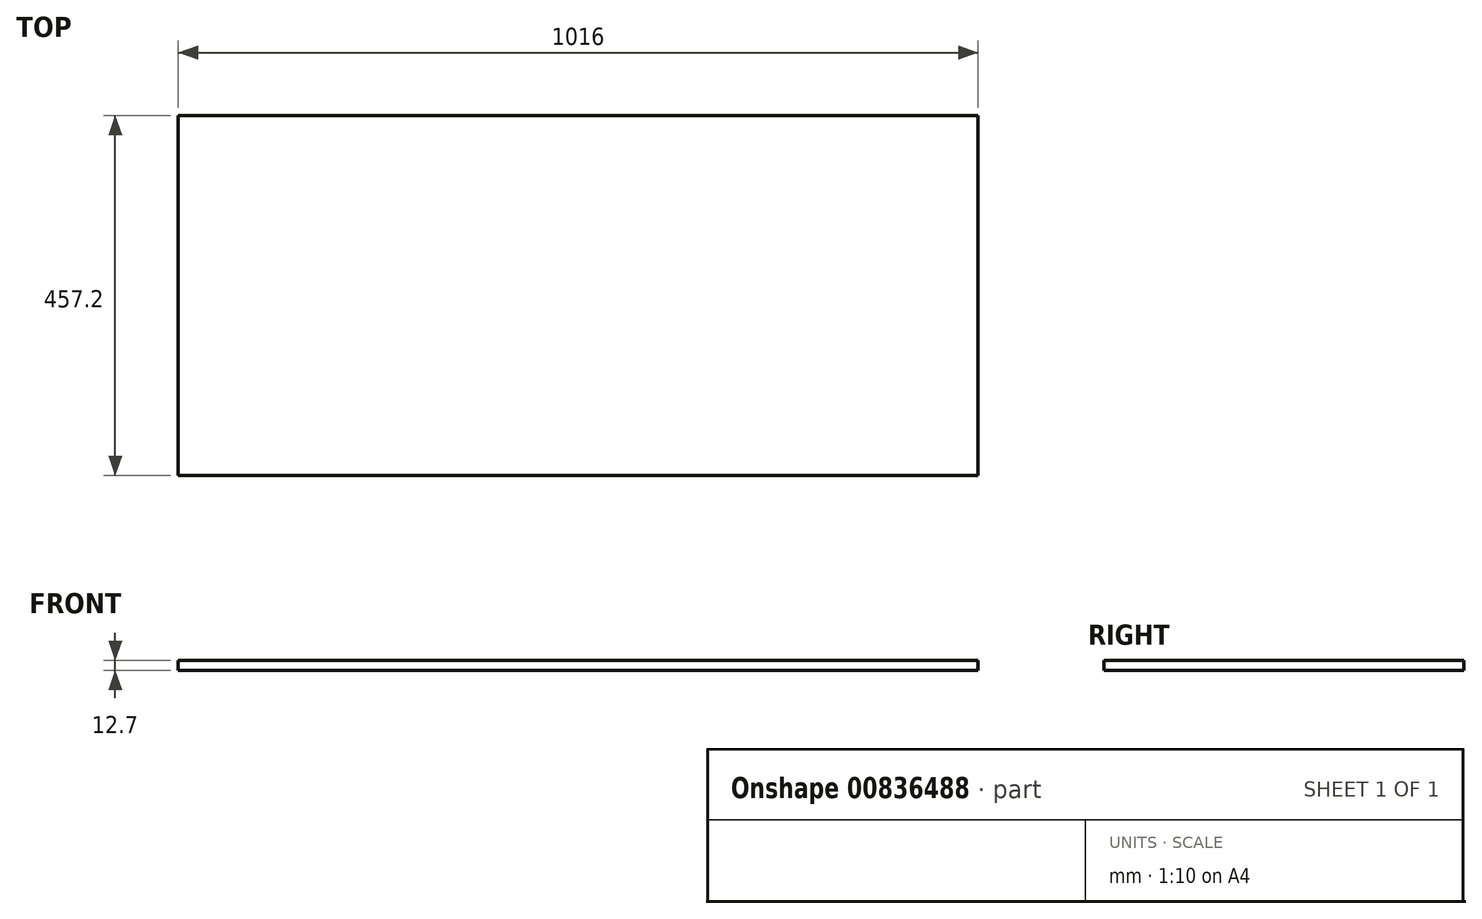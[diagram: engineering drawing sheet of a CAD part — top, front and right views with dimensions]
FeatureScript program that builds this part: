
annotation { "Feature Type Name" : "Feature", "Feature Type Description" : "" }
export const myFeature = defineFeature(function(context is Context, id is Id, definition is map)
    precondition{}
    {
        {
            var Q0;
            Q0=qCreatedBy(makeId("Top.planeOp"),FACE);
            var sketch = newSketch(context, id + "F0", { "sketchPlane" : qUnion([Q0])});
            skLineSegment(sketch, "E0.bottom", {"start": v(0, 0) * mm, "end": v(1016, 0) * mm});
            skLineSegment(sketch, "E0.top", {"start": v(0, -457.2) * mm, "end": v(1016, -457.2) * mm});
            skLineSegment(sketch, "E0.left", {"start": v(0, 0) * mm, "end": v(0, -457.2) * mm});
            skLineSegment(sketch, "E0.right", {"start": v(1016, 0) * mm, "end": v(1016, -457.2) * mm});
            skSolve(sketch);
        }
        {
            var Q0;
            Q0=makeQuery(id+"F0.imprint","IMPRINT",FACE,{"disambiguationData":[TD([[makeQuery(id+"F0.imprint","IMPRINT",EDGE,{"derivedFrom":sQuery(id+"F0.wireOp",EDGE,"E0.bottom")}),-1.0]])]});
            extrude(context, id + "F1", {"entities" : qUnion([Q0]), "depth" : 12.7 * mm, "offsetDistance" : 25.4 * mm});
        }
    });
